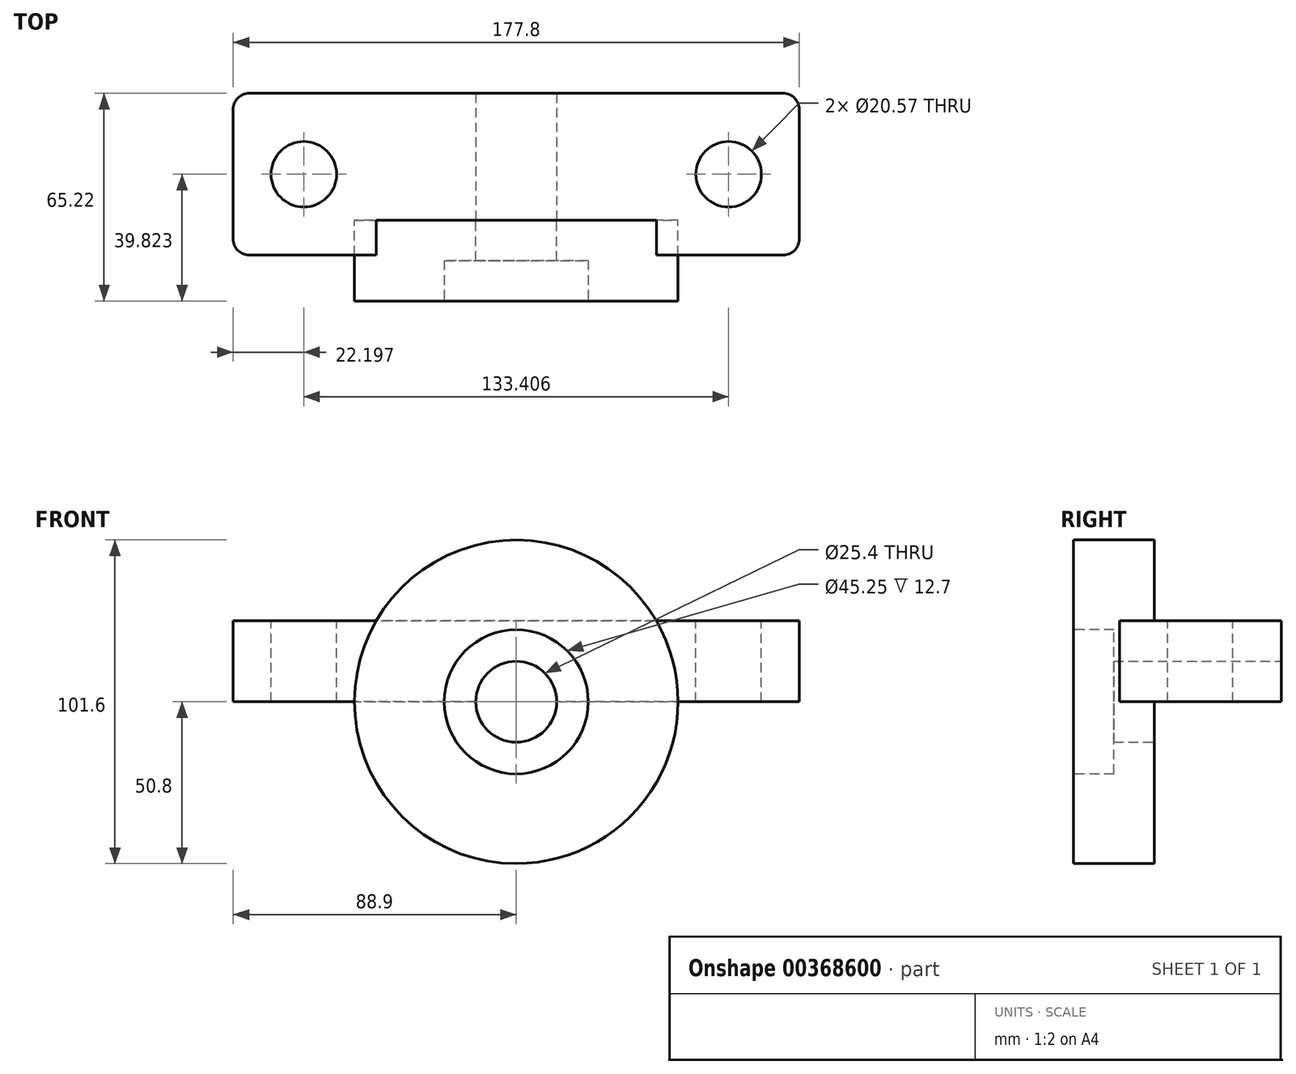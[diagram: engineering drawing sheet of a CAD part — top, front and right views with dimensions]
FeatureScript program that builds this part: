
annotation { "Feature Type Name" : "Feature", "Feature Type Description" : "" }
export const myFeature = defineFeature(function(context is Context, id is Id, definition is map)
    precondition{}
    {
        {
            var Q0;
            Q0=qCreatedBy(makeId("Front.planeOp"),FACE);
            var sketch = newSketch(context, id + "F0", { "sketchPlane" : qUnion([Q0])});
            skCircle(sketch, "E0", {"center": v(0, 0) * mm, "radius": 50.8 * mm});
            skCircle(sketch, "E1", {"center": v(0, 0) * mm, "radius": 12.7 * mm});
            skSolve(sketch);
        }
        {
            var Q0;
            Q0=makeQuery(id+"F0.imprint","IMPRINT",FACE,{"disambiguationData":[TD([[makeQuery(id+"F0.imprint","IMPRINT",EDGE,{"derivedFrom":sQuery(id+"F0.wireOp",EDGE,"E0")}),1.0]])]});
            extrude(context, id + "F1", {"entities" : qUnion([Q0]), "depth" : 25.4 * mm});
        }
        {
            var Q0;
            Q0=qCreatedBy(makeId("Top.planeOp"),FACE);
            var sketch = newSketch(context, id + "F2", { "sketchPlane" : qUnion([Q0])});
            skLineSegment(sketch, "E2.bottom", {"start": v(-88.9, -10.98) * mm, "end": v(88.9, -10.98) * mm});
            skLineSegment(sketch, "E2.top", {"start": v(-88.9, 39.82) * mm, "end": v(88.9, 39.82) * mm});
            skLineSegment(sketch, "E2.left", {"start": v(-88.9, -10.98) * mm, "end": v(-88.9, 39.82) * mm});
            skLineSegment(sketch, "E2.right", {"start": v(88.9, -10.98) * mm, "end": v(88.9, 39.82) * mm});
            skLineSegment(sketch, "E3", {"start": v(0, 0) * mm, "end": v(0, 39.82) * mm, "construction": true});
            skSolve(sketch);
        }
        {
            var Q0;
            Q0=makeQuery(id+"F2.imprint","IMPRINT",FACE,{"disambiguationData":[TD([[makeQuery(id+"F2.imprint","IMPRINT",EDGE,{"derivedFrom":sQuery(id+"F2.wireOp",EDGE,"E2.bottom")}),1.0]])]});
            extrude(context, id + "F3", {"entities" : qUnion([Q0]), "depth" : 25.4 * mm});
        }
        {
            var Q0;
            Q0=makeQuery(id+"F1.opExtrude","SWEPT_BODY",BODY,{"disambiguationData":[OSD([sQuery(id+"F0.wireOp",EDGE,"E0"),sQuery(id+"F0.wireOp",EDGE,"E1")])]});
            var Q1;
            Q1=makeQuery(id+"Fz9N3LtIj3Y4GtS_2.opExtrude","SWEPT_BODY",BODY,{"disambiguationData":[OSD([sQuery(id+"Fj6IW8YYTyOm4j9_1.wireOp",EDGE,"bd638a58-c1e7-4755-98ed-1f227c1695b7.0"),sQuery(id+"Fj6IW8YYTyOm4j9_1.wireOp",EDGE,"d395da0f-da63-4ec0-8de8-44360cae2234.0"),sQuery(id+"Fj6IW8YYTyOm4j9_1.wireOp",EDGE,"d395da0f-da63-4ec0-8de8-44360cae2234.1"),sQuery(id+"Fj6IW8YYTyOm4j9_1.wireOp",EDGE,"d395da0f-da63-4ec0-8de8-44360cae2234.2")])]});
            var Q2;
            Q2=makeQuery(id+"FQRcci72seB8G83_3.opPattern","COPY",BODY,{"derivedFrom":makeQuery(id+"Fz9N3LtIj3Y4GtS_2.opExtrude","SWEPT_BODY",BODY,{"disambiguationData":[OSD([sQuery(id+"Fj6IW8YYTyOm4j9_1.wireOp",EDGE,"bd638a58-c1e7-4755-98ed-1f227c1695b7.0"),sQuery(id+"Fj6IW8YYTyOm4j9_1.wireOp",EDGE,"d395da0f-da63-4ec0-8de8-44360cae2234.0"),sQuery(id+"Fj6IW8YYTyOm4j9_1.wireOp",EDGE,"d395da0f-da63-4ec0-8de8-44360cae2234.1"),sQuery(id+"Fj6IW8YYTyOm4j9_1.wireOp",EDGE,"d395da0f-da63-4ec0-8de8-44360cae2234.2")])]}),"instanceName":"1"});
            var Q3;
            Q3=makeQuery(id+"F3.opExtrude","SWEPT_BODY",BODY,{"disambiguationData":[OSD([sQuery(id+"F2.wireOp",EDGE,"E2.bottom"),sQuery(id+"F2.wireOp",EDGE,"E2.top"),sQuery(id+"F2.wireOp",EDGE,"E2.left"),sQuery(id+"F2.wireOp",EDGE,"E2.right")])]});
            booleanBodies(context, id + "F4", {"operationType" : BooleanOperationType.UNION, "tools" : qUnion([Q0, Q1, Q2, Q3])});
        }
        {
            var Q0;
            {var subQ0=makeQuery(id+"Fz9N3LtIj3Y4GtS_2.opExtrude","CAP_FACE",FACE,{"disambiguationData":[OSD([sQuery(id+"Fj6IW8YYTyOm4j9_1.wireOp",EDGE,"bd638a58-c1e7-4755-98ed-1f227c1695b7.0"),sQuery(id+"Fj6IW8YYTyOm4j9_1.wireOp",EDGE,"d395da0f-da63-4ec0-8de8-44360cae2234.0"),sQuery(id+"Fj6IW8YYTyOm4j9_1.wireOp",EDGE,"d395da0f-da63-4ec0-8de8-44360cae2234.1"),sQuery(id+"Fj6IW8YYTyOm4j9_1.wireOp",EDGE,"d395da0f-da63-4ec0-8de8-44360cae2234.2")])],"isStart":false});Q0=makeQuery(id+"F4.opBoolean","MERGE",FACE,{"derivedFrom":[makeQuery(id+"F1.opExtrude","CAP_FACE",FACE,{"disambiguationData":[OSD([sQuery(id+"F0.wireOp",EDGE,"E0"),sQuery(id+"F0.wireOp",EDGE,"E1")])],"isStart":false}),subQ0,makeQuery(id+"FQRcci72seB8G83_3.opPattern","COPY",FACE,{"derivedFrom":subQ0,"instanceName":"1"})]});}
            var sketch = newSketch(context, id + "F5", { "sketchPlane" : qUnion([Q0])});
            skCircle(sketch, "E4", {"center": v(0, 0) * mm, "radius": 22.62 * mm});
            skSolve(sketch);
        }
        {
            var Q0;
            Q0 = qSketchRegion(id + "F5", true);
            extrude(context, id + "F6", {"entities" : qUnion([Q0]), "operationType" : NewBodyOperationType.REMOVE, "oppositeDirection" : true, "depth" : 12.7 * mm});
        }
        {
            var Q0;
            {var subQ0=makeQuery(id+"Fz9N3LtIj3Y4GtS_2.opExtrude","SWEPT_FACE",FACE,{"disambiguationData":[OSD([sQuery(id+"Fj6IW8YYTyOm4j9_1.wireOp",EDGE,"d395da0f-da63-4ec0-8de8-44360cae2234.0")])]});Q0=makeQuery(id+"F4.opBoolean","MERGE",FACE,{"derivedFrom":[makeQuery(id+"F3.opExtrude","CAP_FACE",FACE,{"disambiguationData":[OSD([sQuery(id+"F2.wireOp",EDGE,"E2.bottom"),sQuery(id+"F2.wireOp",EDGE,"E2.top"),sQuery(id+"F2.wireOp",EDGE,"E2.left"),sQuery(id+"F2.wireOp",EDGE,"E2.right")])],"isStart":false}),subQ0,makeQuery(id+"FQRcci72seB8G83_3.opPattern","COPY",FACE,{"derivedFrom":subQ0,"instanceName":"1"})]});}
            var sketch = newSketch(context, id + "F7", { "sketchPlane" : qUnion([Q0])});
            skCircle(sketch, "E5", {"center": v(-66.7, 14.42) * mm, "radius": 10.29 * mm});
            skCircle(sketch, "E6.MirrorC", {"center": v(66.7, 14.42) * mm, "radius": 10.29 * mm});
            skLineSegment(sketch, "E7", {"start": v(-88.9, 14.42) * mm, "end": v(-66.7, 14.42) * mm, "construction": true});
            skSolve(sketch);
        }
        {
            var Q0;
            Q0 = qSketchRegion(id + "F7", true);
            extrude(context, id + "F8", {"entities" : qUnion([Q0]), "operationType" : NewBodyOperationType.REMOVE, "oppositeDirection" : true, "depth" : 25.4 * mm});
        }
        {
            var Q0;
            Q0=makeQuery(id+"F3.opExtrude","SWEPT_EDGE",EDGE,{"disambiguationData":[OSD([sQuery(id+"F2.wireOp",EDGE,"E2.top"),sQuery(id+"F2.wireOp",EDGE,"E2.right")])]});
            var Q1;
            Q1=makeQuery(id+"F3.opExtrude","SWEPT_EDGE",EDGE,{"disambiguationData":[OSD([sQuery(id+"F2.wireOp",EDGE,"E2.top"),sQuery(id+"F2.wireOp",EDGE,"E2.left")])]});
            var Q2;
            Q2=makeQuery(id+"F3.opExtrude","SWEPT_EDGE",EDGE,{"disambiguationData":[OSD([sQuery(id+"F2.wireOp",EDGE,"E2.bottom"),sQuery(id+"F2.wireOp",EDGE,"E2.left")])]});
            var Q3;
            Q3=makeQuery(id+"F3.opExtrude","SWEPT_EDGE",EDGE,{"disambiguationData":[OSD([sQuery(id+"F2.wireOp",EDGE,"E2.bottom"),sQuery(id+"F2.wireOp",EDGE,"E2.right")])]});
            fillet(context, id + "F9", {"entities" : qUnion([Q0, Q1, Q2, Q3]), "radius" : 5.08 * mm, "tangentPropagation" : true, "allowEdgeOverflow" : false});
        }
        {
            var Q0;
            Q0=makeQuery(id+"F1.opExtrude","CAP_FACE",FACE,{"disambiguationData":[OSD([sQuery(id+"F0.wireOp",EDGE,"E0"),sQuery(id+"F0.wireOp",EDGE,"E1")])],"isStart":false});
            var sketch = newSketch(context, id + "F10", { "sketchPlane" : qUnion([Q0])});
            skSolve(sketch);
        }
        {
            var Q0;
            Q0=makeQuery(id+"F10.imprint","IMPRINT",FACE,{"disambiguationData":[TD([[makeQuery(id+"F10.imprint","IMPRINT",EDGE,{"derivedFrom":makeQuery(id+"F1.opExtrude","CAP_EDGE",EDGE,{"disambiguationData":[OSD([sQuery(id+"F0.wireOp",EDGE,"E0")])],"isStart":false})}),1.0]])]});
            var sketch = newSketch(context, id + "F11", { "sketchPlane" : qUnion([Q0])});
            skCircle(sketch, "E8", {"center": v(0, 0) * mm, "radius": 12.7 * mm});
            skSolve(sketch);
        }
        {
            var Q0;
            Q0 = qSketchRegion(id + "F11", true);
            extrude(context, id + "F12", {"entities" : qUnion([Q0]), "operationType" : NewBodyOperationType.REMOVE, "oppositeDirection" : true, "depth" : 76.2 * mm});
        }
    });
